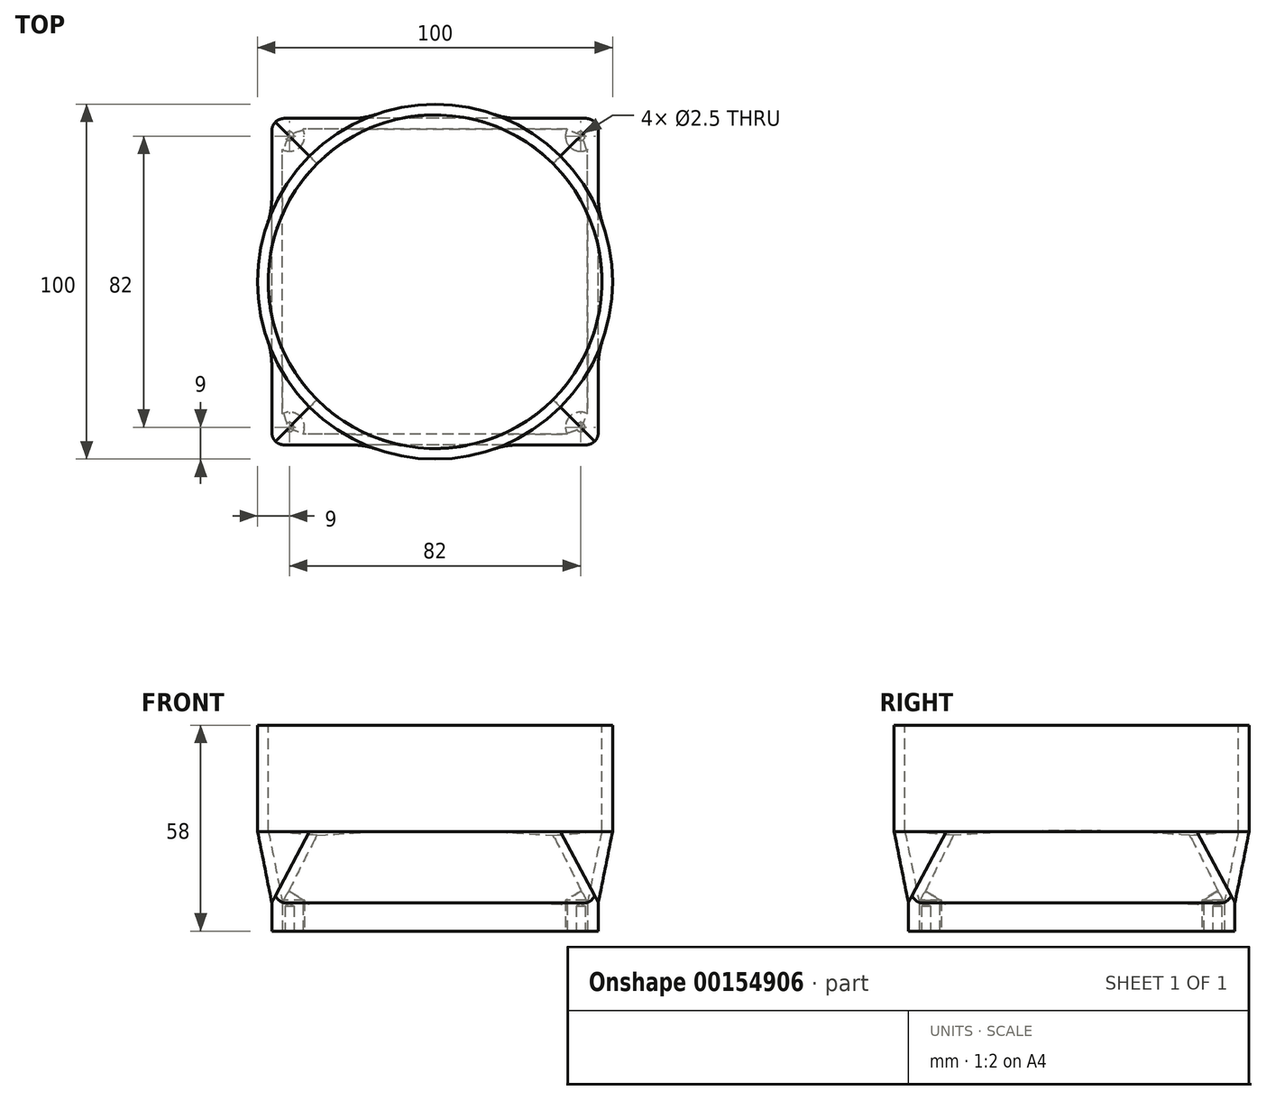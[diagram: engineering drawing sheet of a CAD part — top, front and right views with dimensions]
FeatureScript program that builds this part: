
annotation { "Feature Type Name" : "Feature", "Feature Type Description" : "" }
export const myFeature = defineFeature(function(context is Context, id is Id, definition is map)
    precondition{}
    {
        {
            var Q0;
            Q0=qCreatedBy(makeId("Top.planeOp"),FACE);
            var sketch = newSketch(context, id + "F0", { "sketchPlane" : qUnion([Q0])});
            skLineSegment(sketch, "E0.bottom", {"start": v(46, -46) * mm, "end": v(-46, -46) * mm});
            skLineSegment(sketch, "E0.top", {"start": v(46, 46) * mm, "end": v(-46, 46) * mm});
            skLineSegment(sketch, "E0.left", {"start": v(46, -46) * mm, "end": v(46, 46) * mm});
            skLineSegment(sketch, "E0.right", {"start": v(-46, -46) * mm, "end": v(-46, 46) * mm});
            skPoint(sketch, "E0.middle", {"position": v(0, 0) * mm});
            skSolve(sketch);
        }
        {
            var Q0;
            Q0=makeQuery(id+"F0.imprint","IMPRINT",FACE,{"disambiguationData":[TD([[makeQuery(id+"F0.imprint","IMPRINT",EDGE,{"derivedFrom":sQuery(id+"F0.wireOp",EDGE,"E0.bottom")}),-1.0]])]});
            extrude(context, id + "F1", {"entities" : qUnion([Q0]), "depth" : 8 * mm});
        }
        {
            var Q0;
            Q0=makeQuery(id+"F1.opExtrude","CAP_FACE",FACE,{"disambiguationData":[OSD([sQuery(id+"F0.wireOp",EDGE,"E0.bottom"),sQuery(id+"F0.wireOp",EDGE,"E0.top"),sQuery(id+"F0.wireOp",EDGE,"E0.left"),sQuery(id+"F0.wireOp",EDGE,"E0.right")])],"isStart":false});
            cPlane(context, id + "F2", {"entities" : qUnion([Q0]), "cplaneType" : CPlaneType.OFFSET, "offset" : 20 * mm, "width" : 150 * mm, "height" : 150 * mm});
        }
        {
            var Q0;
            Q0=qCreatedBy(id+"F2.planeOp",FACE);
            var sketch = newSketch(context, id + "F3", { "sketchPlane" : qUnion([Q0])});
            skCircle(sketch, "E1", {"center": v(0, 0) * mm, "radius": 50 * mm});
            skSolve(sketch);
        }
        {
            var Q1;
            Q1=makeQuery(id+"F1.opExtrude","CAP_FACE",FACE,{"disambiguationData":[OSD([sQuery(id+"F0.wireOp",EDGE,"E0.bottom"),sQuery(id+"F0.wireOp",EDGE,"E0.top"),sQuery(id+"F0.wireOp",EDGE,"E0.left"),sQuery(id+"F0.wireOp",EDGE,"E0.right")])],"isStart":false});
            var Q2;
            Q2=makeQuery(id+"F3.imprint","IMPRINT",FACE,{"disambiguationData":[TD([[makeQuery(id+"F3.imprint","IMPRINT",EDGE,{"derivedFrom":sQuery(id+"F3.wireOp",EDGE,"E1")}),1.0]])]});
            loft(context, id + "F4", {"operationType" : NewBodyOperationType.ADD, "sheetProfilesArray" : [{ "sheetProfileEntities" : qUnion([Q1]) }, { "sheetProfileEntities" : qUnion([Q2]) }]});
        }
        {
            var Q0;
            Q0=makeQuery(id+"F1.opExtrude","CAP_FACE",FACE,{"disambiguationData":[OSD([sQuery(id+"F0.wireOp",EDGE,"E0.bottom"),sQuery(id+"F0.wireOp",EDGE,"E0.top"),sQuery(id+"F0.wireOp",EDGE,"E0.left"),sQuery(id+"F0.wireOp",EDGE,"E0.right")])],"isStart":true});
            var sketch = newSketch(context, id + "F5", { "sketchPlane" : qUnion([Q0])});
            skLineSegment(sketch, "E2.bottom", {"start": v(-41, -41) * mm, "end": v(41, -41) * mm});
            skLineSegment(sketch, "E2.top", {"start": v(-41, 41) * mm, "end": v(41, 41) * mm});
            skLineSegment(sketch, "E2.left", {"start": v(-41, -41) * mm, "end": v(-41, 41) * mm});
            skLineSegment(sketch, "E2.right", {"start": v(41, -41) * mm, "end": v(41, 41) * mm});
            skPoint(sketch, "E2.middle", {"position": v(0, 0) * mm});
            skSolve(sketch);
        }
        {
            var Q0;
            Q0=sQuery(id+"F5.wireOp",VERTEX,"E2.right.end");
            var Q1;
            Q1=sQuery(id+"F5.wireOp",VERTEX,"E2.left.end");
            var Q2;
            Q2=sQuery(id+"F5.wireOp",VERTEX,"E2.left.start");
            var Q3;
            Q3=sQuery(id+"F5.wireOp",VERTEX,"E2.right.start");
            var Q4;
            Q4=makeQuery(id+"F1.opExtrude","SWEPT_BODY",BODY,{"disambiguationData":[OSD([sQuery(id+"F0.wireOp",EDGE,"E0.bottom"),sQuery(id+"F0.wireOp",EDGE,"E0.top"),sQuery(id+"F0.wireOp",EDGE,"E0.left"),sQuery(id+"F0.wireOp",EDGE,"E0.right")])]});
            hole(context, id + "F6", {"style" : HoleStyle.SIMPLE, "endStyle" : HoleEndStyle.BLIND, "holeDiameter" : 2.5 * mm, "holeDepth" : 7 * mm, "locations" : qUnion([Q0, Q1, Q2, Q3]), "scope" : qUnion([Q4])});
        }
        {
            var Q0;
            Q0=makeQuery(id+"F4.opLoft","CAP_FACE",FACE,{"disambiguationData":[OSD([makeQuery(id+"F3.imprint","IMPRINT",FACE,{"disambiguationData":[TD([[makeQuery(id+"F3.imprint","IMPRINT",EDGE,{"derivedFrom":sQuery(id+"F3.wireOp",EDGE,"E1")}),1.0]])]})])],"isStart":true});
            extrude(context, id + "F7", {"entities" : qUnion([Q0]), "operationType" : NewBodyOperationType.ADD, "depth" : 30 * mm});
        }
        {
            var Q0;
            Q0=makeQuery(id+"F1.opExtrude","CAP_FACE",FACE,{"disambiguationData":[OSD([sQuery(id+"F0.wireOp",EDGE,"E0.bottom"),sQuery(id+"F0.wireOp",EDGE,"E0.top"),sQuery(id+"F0.wireOp",EDGE,"E0.left"),sQuery(id+"F0.wireOp",EDGE,"E0.right")])],"isStart":true});
            var Q1;
            Q1=makeQuery(id+"F7.opExtrude","CAP_FACE",FACE,{"disambiguationData":[OSD([makeQuery(id+"F3.imprint","IMPRINT",FACE,{"disambiguationData":[TD([[makeQuery(id+"F3.imprint","IMPRINT",EDGE,{"derivedFrom":sQuery(id+"F3.wireOp",EDGE,"E1")}),1.0]])]})])],"isStart":false});
            shell(context, id + "F8", {"entities" : qUnion([Q0, Q1]), "thickness" : 3 * mm});
        }
        {
            var Q0;
            Q0=makeQuery(id+"F1.opExtrude","SWEPT_EDGE",EDGE,{"disambiguationData":[OSD([sQuery(id+"F0.wireOp",EDGE,"E0.top"),sQuery(id+"F0.wireOp",EDGE,"E0.left")])]});
            var Q1;
            Q1=makeQuery(id+"F1.opExtrude","SWEPT_EDGE",EDGE,{"disambiguationData":[OSD([sQuery(id+"F0.wireOp",EDGE,"E0.bottom"),sQuery(id+"F0.wireOp",EDGE,"E0.left")])]});
            var Q2;
            Q2=makeQuery(id+"F1.opExtrude","SWEPT_EDGE",EDGE,{"disambiguationData":[OSD([sQuery(id+"F0.wireOp",EDGE,"E0.bottom"),sQuery(id+"F0.wireOp",EDGE,"E0.right")])]});
            var Q3;
            Q3=makeQuery(id+"F1.opExtrude","SWEPT_EDGE",EDGE,{"disambiguationData":[OSD([sQuery(id+"F0.wireOp",EDGE,"E0.top"),sQuery(id+"F0.wireOp",EDGE,"E0.right")])]});
            fillet(context, id + "F9", {"entities" : qUnion([Q0, Q1, Q2, Q3]), "radius" : 3.5 * mm, "tangentPropagation" : true, "allowEdgeOverflow" : false});
        }
    });
